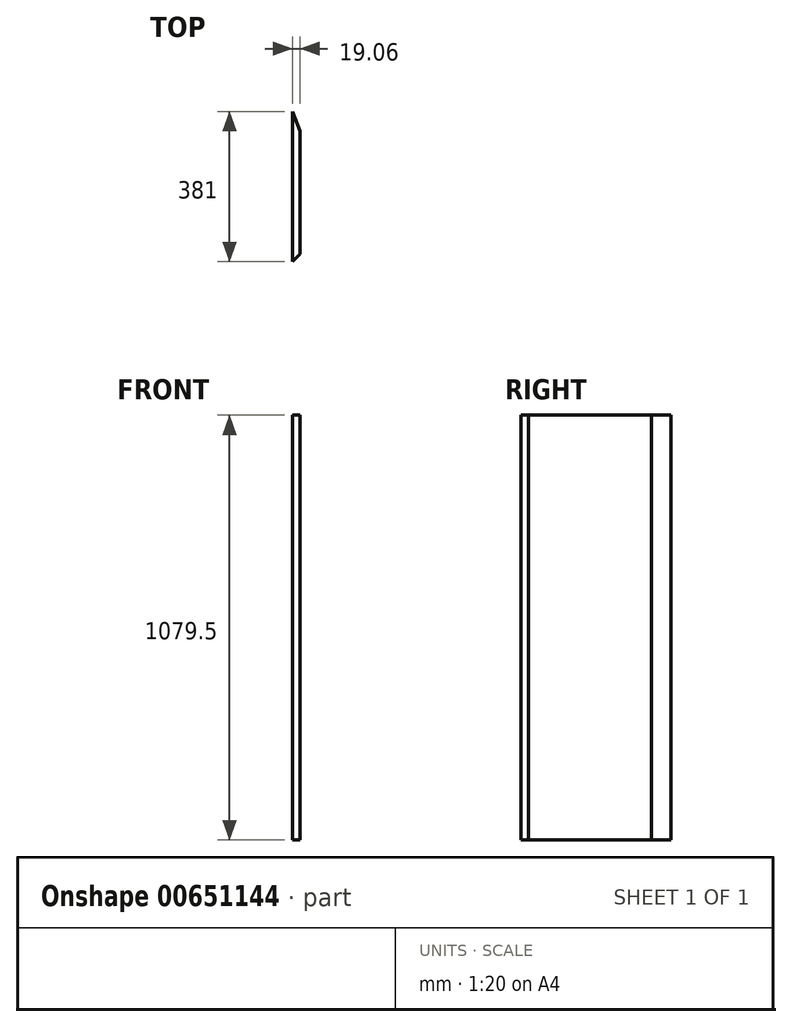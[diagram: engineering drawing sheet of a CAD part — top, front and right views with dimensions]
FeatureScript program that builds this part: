
annotation { "Feature Type Name" : "Feature", "Feature Type Description" : "" }
export const myFeature = defineFeature(function(context is Context, id is Id, definition is map)
    precondition{}
    {
        {
            var Q0;
            Q0=qCreatedBy(makeId("Top.planeOp"),FACE);
            var sketch = newSketch(context, id + "F0", { "sketchPlane" : qUnion([Q0])});
            skLineSegment(sketch, "E0", {"start": v(-9.53, -183.02) * mm, "end": v(-9.53, 197.98) * mm});
            skLineSegment(sketch, "E1.0", {"start": v(9.53, -163.97) * mm, "end": v(9.53, 149) * mm});
            skLineSegment(sketch, "E2", {"start": v(-9.52, 197.98) * mm, "end": v(9.53, 149) * mm});
            skLineSegment(sketch, "E3", {"start": v(9.53, -163.97) * mm, "end": v(-9.53, -183.02) * mm});
            skSolve(sketch);
        }
        {
            var Q0;
            Q0=makeQuery(id+"F0.imprint","IMPRINT",FACE,{"disambiguationData":[TD([[makeQuery(id+"F0.imprint","IMPRINT",EDGE,{"derivedFrom":sQuery(id+"F0.wireOp",EDGE,"E0")}),-1.0]])]});
            extrude(context, id + "F1", {"entities" : qUnion([Q0]), "depth" : 1079.5 * mm, "offsetDistance" : 25.4 * mm});
        }
    });
